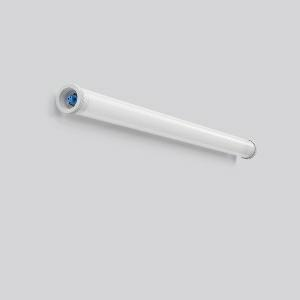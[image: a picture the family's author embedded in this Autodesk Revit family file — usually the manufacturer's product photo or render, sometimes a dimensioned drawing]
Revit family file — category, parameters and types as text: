
# Revit family: planox_tube_601071_002_730hf_5a42
name_source: partatom
category: Lighting Fixtures
units: mm (PartAtom-declared; Revit-internal decimal feet)

## family parameters
Cut with Voids When Loaded = No
Host = Face
Light Source = No
Part Type = Normal
Room Calculation Point = No
Round Connector Dimension = Use Diameter
Shared = No

## types (1)
- PLANOX TUBE (1 x LED Modul 840, 5350 lm, 4000)
    Apparent Load = 39 VA
    CIE Flux Codes = 42 71 89 90 100
    Color Rendering = 80
    Color Temperature = 4000
    Default Elevation = 1800 mm
    Description = Series: PLANOX TUBE
Robust protective tube luminaire for tough requirements. Rack made of sheet steel, white powder coated. End caps made of plastic (polyamide) grey. Diffuser made of plastic (polycarbonate), opal, shockproof. Symmetrical light distribution. Homogeneous light distribution. With accessories for wall, ceiling or pendant mounting. Mounting set must be ordered separately. Luminaire with limited surface temperature in accordance with EN 60598-2-24 for use in environments in which a deposit of conductive dust on the luminaire can be expected. Qualified for use in the food and drink industry. Suitable for lighting in public car parks and public off-street parking spaces according to DIN 67528. Environmentally friendly and resource-saving due to replaceable components. 
Colour: white
Diameter: 78 mm
Length: 1349 mm
Lamp: LED
Socket: without socket
Colour temperature: 4000K
Colour rendering index (CRI): 83
System power: 39 W
Rated luminous flux: 5350 lm
Luminous efficiency: 137 lm/W
Control gear: Dimmable Bluetooth converter
Protection class: I
Type of protection: IP 67
    Height = 0 mm  [stored 0 ft]
    Lamp = 1 x LED Modul 840
    Lamp Light Flux = 5350 lm
    Lamp count = 1
    Length = 1349 mm
    Lifetime = 50000 h
    Luminous efficacy = 137 lm/W
    Manufacturer = RZB
    ModVariant = No
    Model = 601071.002.730HF
    Mounting Place = Ceiling, Wall
    Mounting Type = Surface mounted
    Number of Poles = 1
    OnlyDefault = Yes
    Power Factor = 1
    Product Name = PLANOX TUBE
    Product group = Surface mounted luminaires for moist/humid enviroments
    ProductGroupID = 308
    Protection Class = Protection class I
    Protection Degree = Degree of protection
    RLX_Detail_Level = 1
    RLX_Emergency_Light_Flux = 0 lm
    RLX_Emergency_Type = 0
    RLX_Emergency_Type_DB = No
    RlxData = <blob elided: 33609 chars, md5=1281ebbb>
    Socket = socket
    Standby Power = 0 W
    System Light Flux = 5350 lm
    System Power = 39 W
    Type Comments = Product without accessories
    Type Image = 601071.002.jpg
    URL = http://relux.com
    VarID = ---
    Voltage = 230 V
    Voltage Range = 220-240 V
    Weight = 0.00 kg
    Width = 0 mm  [stored 0 ft]

note: [stored X ft] marks values corroborated as IEEE doubles in the binary element streams (Revit-internal decimal feet)

## geometry (parser evidence)
native form markers: Blend x4, Sweep x11
no freeform markers — native parametric forms only
